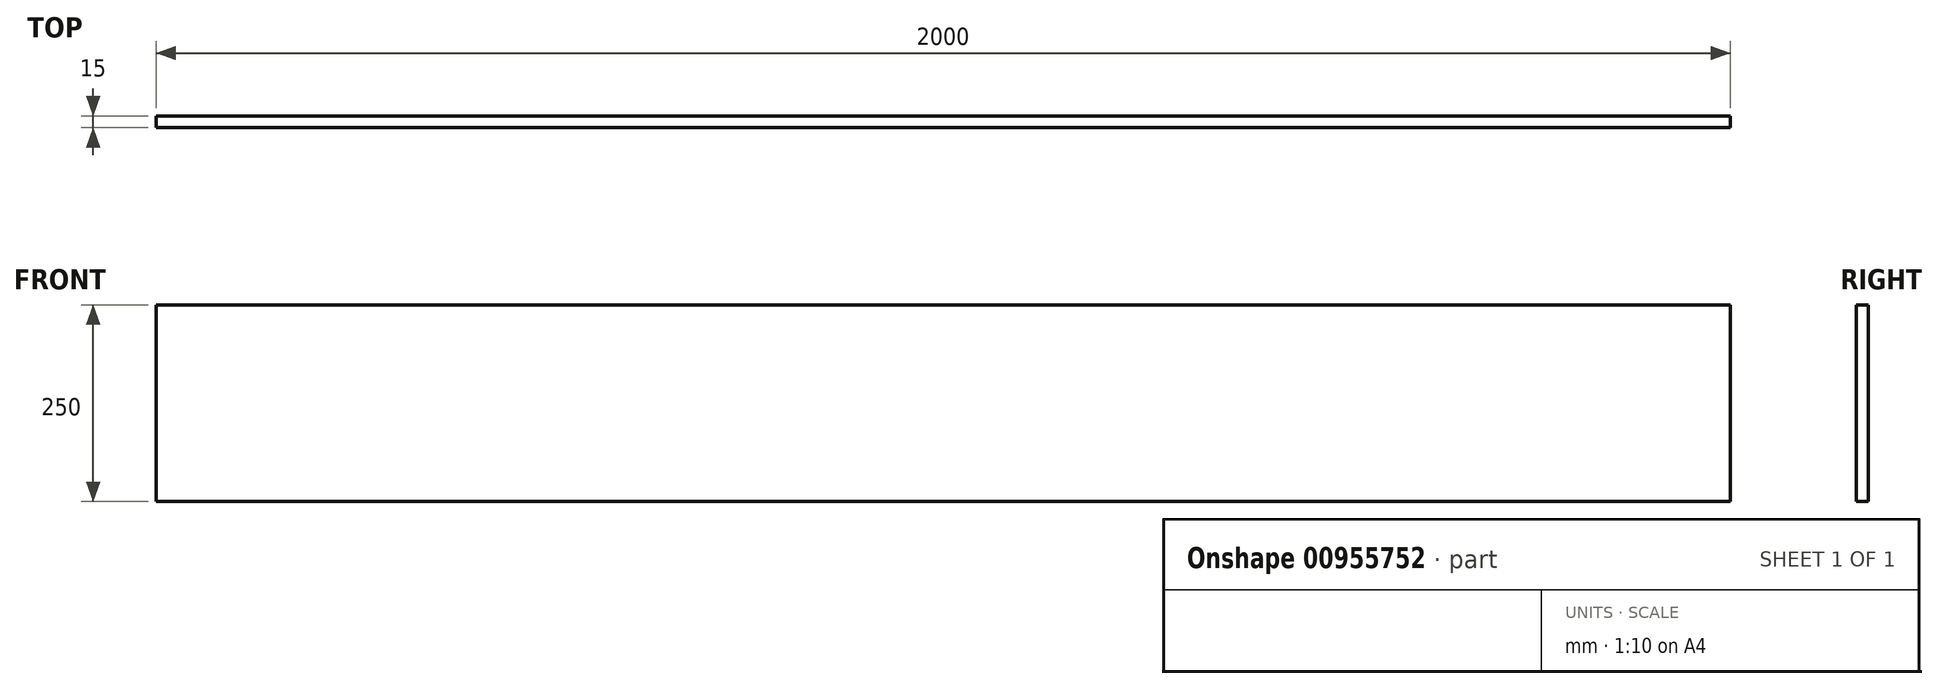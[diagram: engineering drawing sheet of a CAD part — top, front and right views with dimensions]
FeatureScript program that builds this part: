
annotation { "Feature Type Name" : "Feature", "Feature Type Description" : "" }
export const myFeature = defineFeature(function(context is Context, id is Id, definition is map)
    precondition{}
    {
        {
            var Q0;
            Q0=qCreatedBy(makeId("Front.planeOp"),FACE);
            var sketch = newSketch(context, id + "F0", { "sketchPlane" : qUnion([Q0])});
            skLineSegment(sketch, "E0.bottom", {"start": v(0, 0) * mm, "end": v(2000, 0) * mm});
            skLineSegment(sketch, "E0.top", {"start": v(0, -250) * mm, "end": v(2000, -250) * mm});
            skLineSegment(sketch, "E0.left", {"start": v(0, 0) * mm, "end": v(0, -250) * mm});
            skLineSegment(sketch, "E0.right", {"start": v(2000, 0) * mm, "end": v(2000, -250) * mm});
            skSolve(sketch);
        }
        {
            var Q0;
            Q0 = qSketchRegion(id + "F0", true);
            extrude(context, id + "F1", {"entities" : qUnion([Q0]), "depth" : 15 * mm, "offsetDistance" : 25 * mm});
        }
    });
